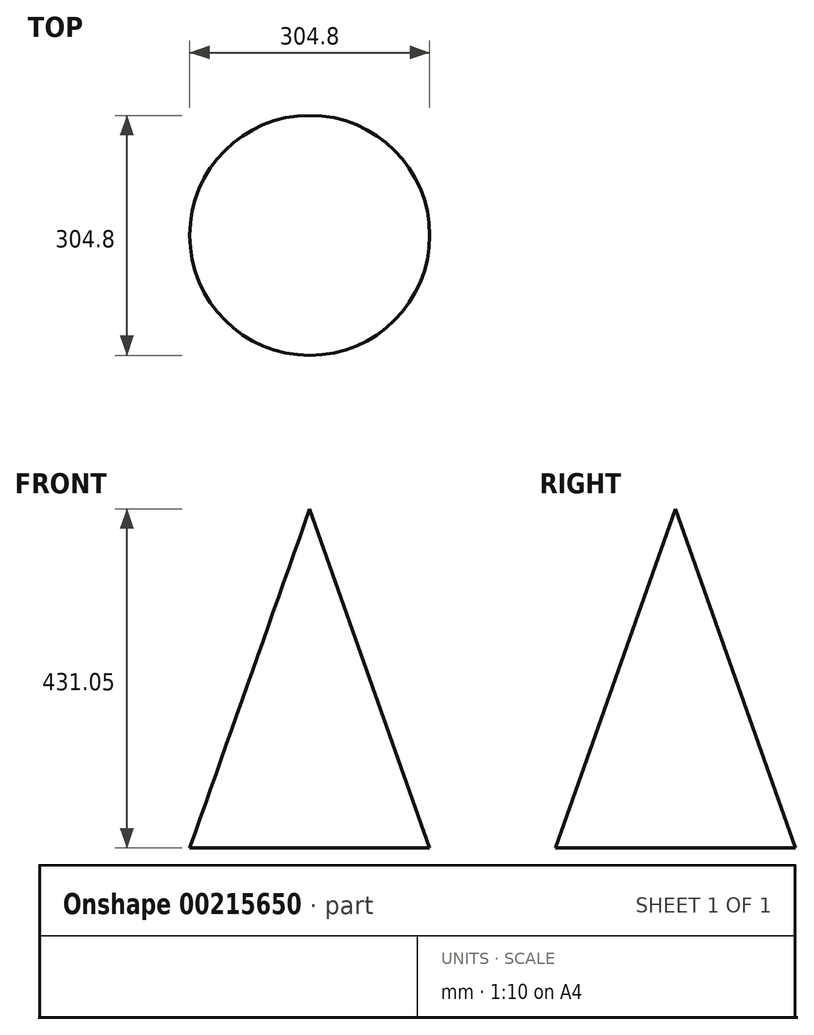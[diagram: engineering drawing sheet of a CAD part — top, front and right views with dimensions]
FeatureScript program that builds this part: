
annotation { "Feature Type Name" : "Feature", "Feature Type Description" : "" }
export const myFeature = defineFeature(function(context is Context, id is Id, definition is map)
    precondition{}
    {
        {
            var Q0;
            Q0=qCreatedBy(makeId("Front.planeOp"),FACE);
            var sketch = newSketch(context, id + "F0", { "sketchPlane" : qUnion([Q0])});
            skLineSegment(sketch, "E0", {"start": v(0, 215.53) * mm, "end": v(0, 53.4) * mm, "construction": true});
            skLineSegment(sketch, "E1", {"start": v(0, 215.53) * mm, "end": v(0, -18.83) * mm, "construction": true});
            skLineSegment(sketch, "E2", {"start": v(76.2, 215.53) * mm, "end": v(152.4, 0) * mm});
            skLineSegment(sketch, "E3", {"start": v(76.2, 215.53) * mm, "end": v(0, 215.53) * mm});
            skLineSegment(sketch, "E4", {"start": v(0, 215.53) * mm, "end": v(0, 0) * mm});
            skLineSegment(sketch, "E5", {"start": v(0, 0) * mm, "end": v(152.4, 0) * mm});
            skSolve(sketch);
        }
        {
            var Q0;
            Q0 = qSketchRegion(id + "F0", true);
            var Q1;
            Q1=sQuery(id+"F0.wireOp",EDGE,"E1");
            revolve(context, id + "F1", {"entities" : qUnion([Q0]), "axis" : qUnion([Q1]), "revolveType" : RevolveType.FULL});
        }
        {
            var Q0;
            Q0=qCreatedBy(makeId("Front.planeOp"),FACE);
            var sketch = newSketch(context, id + "F2", { "sketchPlane" : qUnion([Q0])});
            skLineSegment(sketch, "E6", {"start": v(0, 195.72) * mm, "end": v(0, 390.37) * mm, "construction": true});
            skLineSegment(sketch, "E7", {"start": v(76.2, 215.53) * mm, "end": v(0, 431.05) * mm});
            skLineSegment(sketch, "E8", {"start": v(0, 431.05) * mm, "end": v(0, 215.53) * mm});
            skLineSegment(sketch, "E9", {"start": v(0, 215.53) * mm, "end": v(76.2, 215.53) * mm});
            skSolve(sketch);
        }
        {
            var Q0;
            Q0 = qSketchRegion(id + "F2", true);
            var Q1;
            Q1=sQuery(id+"F2.wireOp",EDGE,"E6");
            revolve(context, id + "F3", {"operationType" : NewBodyOperationType.ADD, "entities" : qUnion([Q0]), "axis" : qUnion([Q1]), "revolveType" : RevolveType.FULL});
        }
    });
